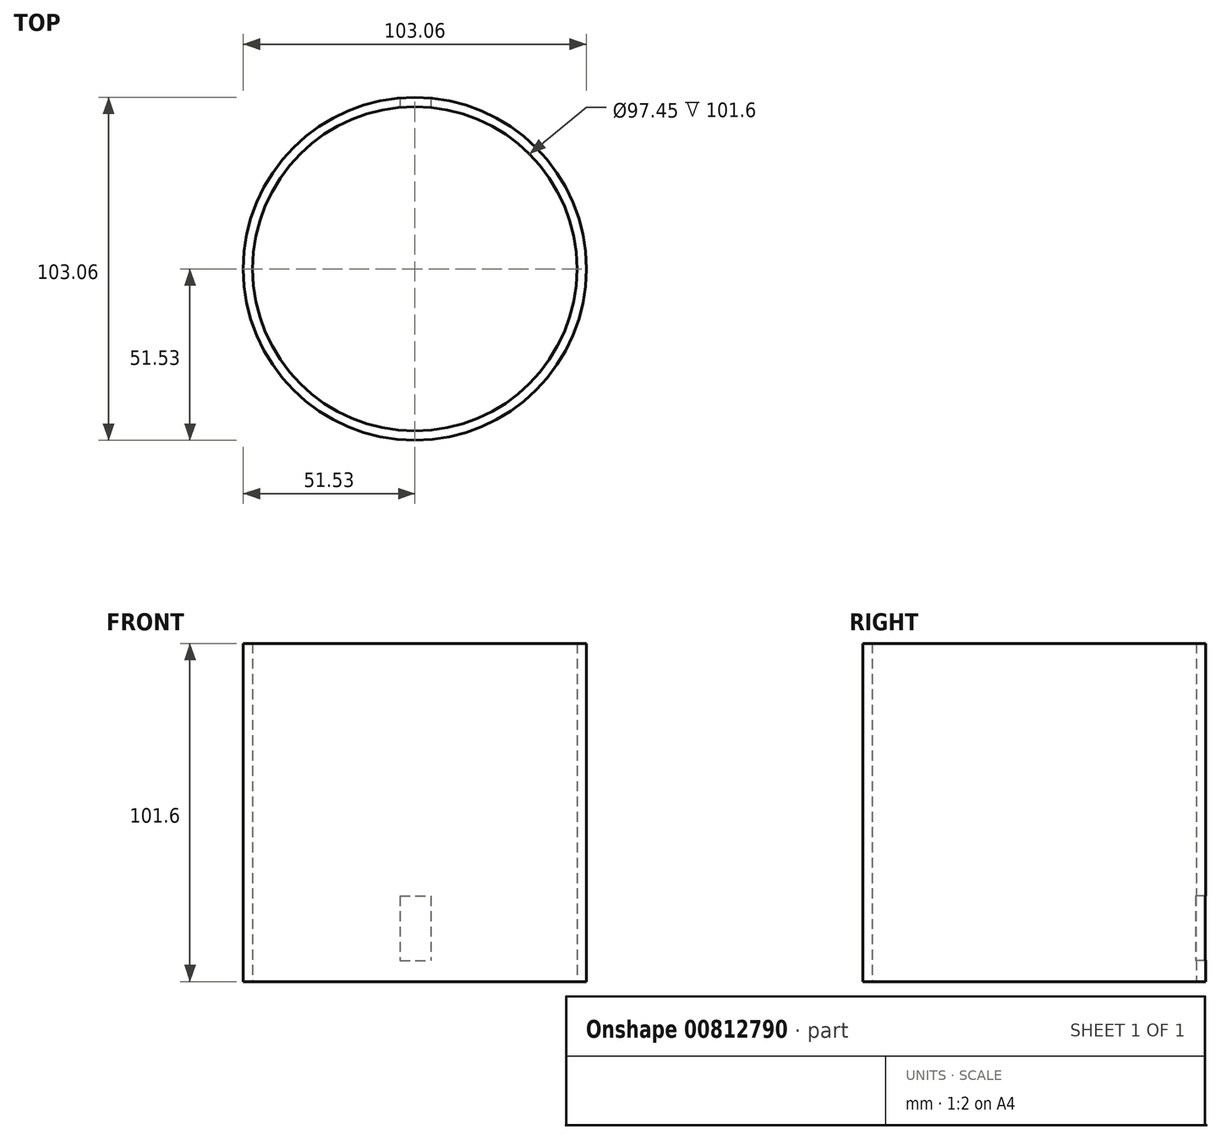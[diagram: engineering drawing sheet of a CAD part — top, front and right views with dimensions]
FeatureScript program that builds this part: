
annotation { "Feature Type Name" : "Feature", "Feature Type Description" : "" }
export const myFeature = defineFeature(function(context is Context, id is Id, definition is map)
    precondition{}
    {
        {
            var Q0;
            Q0=qCreatedBy(makeId("Top.planeOp"),FACE);
            var sketch = newSketch(context, id + "F0", { "sketchPlane" : qUnion([Q0])});
            skCircle(sketch, "E0", {"center": v(0, 0) * mm, "radius": 51.53 * mm});
            skCircle(sketch, "E1", {"center": v(0, 0) * mm, "radius": 48.72 * mm});
            skSolve(sketch);
        }
        {
            var Q0;
            Q0=makeQuery(id+"F0.imprint","IMPRINT",FACE,{"disambiguationData":[TD([[makeQuery(id+"F0.imprint","IMPRINT",EDGE,{"derivedFrom":sQuery(id+"F0.wireOp",EDGE,"E0")}),1.0]])]});
            extrude(context, id + "F1", {"entities" : qUnion([Q0]), "depth" : 101.6 * mm, "offsetDistance" : 25.4 * mm});
        }
        {
            var Q0;
            Q0=qCreatedBy(makeId("Front.planeOp"),FACE);
            var sketch = newSketch(context, id + "F2", { "sketchPlane" : qUnion([Q0])});
            skLineSegment(sketch, "E2.bottom", {"start": v(-4.4, 25.71) * mm, "end": v(4.84, 25.71) * mm});
            skLineSegment(sketch, "E2.top", {"start": v(-4.4, 6.36) * mm, "end": v(4.84, 6.36) * mm});
            skLineSegment(sketch, "E2.left", {"start": v(-4.4, 25.71) * mm, "end": v(-4.4, 6.36) * mm});
            skLineSegment(sketch, "E2.right", {"start": v(4.84, 25.71) * mm, "end": v(4.84, 6.36) * mm});
            skSolve(sketch);
        }
        {
            var Q0;
            Q0 = qSketchRegion(id + "F2", true);
            extrude(context, id + "F3", {"entities" : qUnion([Q0]), "operationType" : NewBodyOperationType.REMOVE, "oppositeDirection" : true, "depth" : 127 * mm, "offsetDistance" : 25.4 * mm});
        }
    });
